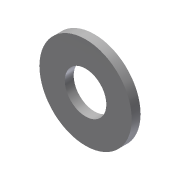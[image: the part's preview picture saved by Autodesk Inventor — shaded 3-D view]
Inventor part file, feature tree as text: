
AUTODESK INVENTOR PART (.ipt)
format: ipt  version: 2013 (Build 170138000, 138)  size: 74,752 bytes
history: native  units: in
note: dims shown in document units (in); Inventor stores cm internally (conversion verified against a paired STEP export)
features: extrude x1, sketch x1
ambient origin geometry x8: Origin, YZ Plane, XZ Plane, XY Plane, X Axis, Y Axis, Z Axis, Center Point
bodies: Solid1 (feature_tree)
feature tree (2):
  extrude  "Extrusion1"  Depth=0.625in
  sketch  "Sketch2"  dims[d0=0.2812in d1=0.625in d2=0.06in d3=0.0in]
